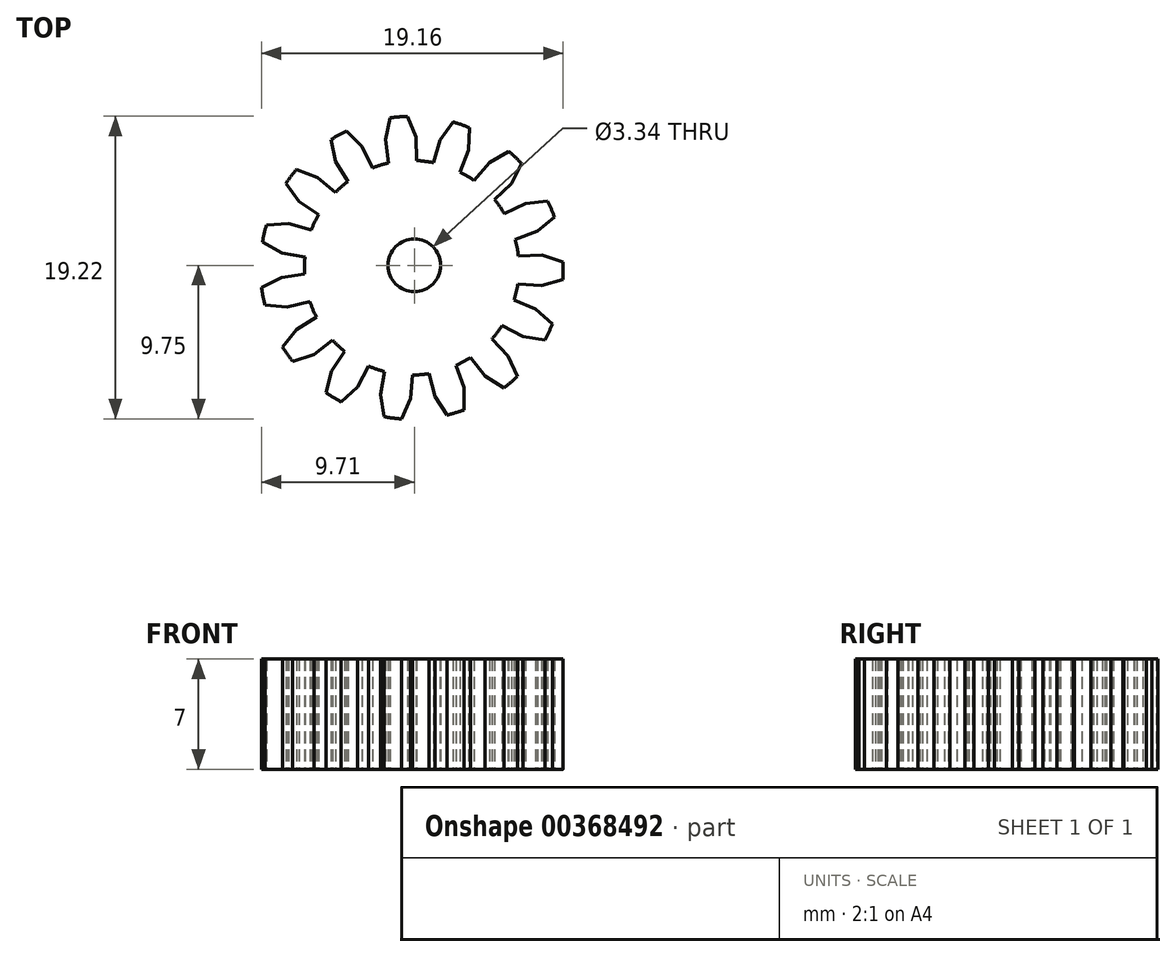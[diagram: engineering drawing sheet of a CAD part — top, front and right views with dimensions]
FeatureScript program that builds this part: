
annotation { "Feature Type Name" : "Feature", "Feature Type Description" : "" }
export const myFeature = defineFeature(function(context is Context, id is Id, definition is map)
    precondition{}
    {
        {
            var Q0;
            Q0=qCreatedBy(makeId("Top.planeOp"),FACE);
            var sketch = newSketch(context, id + "F0", { "sketchPlane" : qUnion([Q0])});
            skLineSegment(sketch, "E0", {"start": v(-0.17, -0.15) * mm, "end": v(4.15, 8.45) * mm, "construction": true});
            skLineSegment(sketch, "E1", {"start": v(-0.17, -0.15) * mm, "end": v(7.27, 5.95) * mm, "construction": true});
            skLineSegment(sketch, "E2", {"start": v(-0.17, -0.15) * mm, "end": v(6.41, 6.87) * mm, "construction": true});
            skLineSegment(sketch, "E3", {"start": v(5.1, 4.17) * mm, "end": v(6.17, 5.21) * mm});
            skLineSegment(sketch, "E4", {"start": v(6.17, 5.21) * mm, "end": v(6.8, 6.48) * mm});
            skLineSegment(sketch, "E5.MirrorCS", {"start": v(5.71, 3.3) * mm, "end": v(7.06, 3.94) * mm});
            skLineSegment(sketch, "E6.MirrorCS", {"start": v(4.77, 6.53) * mm, "end": v(5.99, 7.24) * mm});
            skArc(sketch, "E7", {"start": v(5.99, 7.24) * mm, "mid": v(6.41, 6.87) * mm, "end": v(6.8, 6.48) * mm});
            skLineSegment(sketch, "E8.1.0", {"start": v(6.6, 0.6) * mm, "end": v(8.1, 0.65) * mm});
            skLineSegment(sketch, "E8.1.1", {"start": v(7.06, 3.94) * mm, "end": v(8.46, 4.1) * mm});
            skLineSegment(sketch, "E8.1.2", {"start": v(7.8, 2.17) * mm, "end": v(8.9, 3.06) * mm});
            skArc(sketch, "E8.1.3", {"start": v(8.46, 4.1) * mm, "mid": v(8.7, 3.59) * mm, "end": v(8.9, 3.06) * mm});
            skLineSegment(sketch, "E8.1.4", {"start": v(6.4, 1.65) * mm, "end": v(7.8, 2.17) * mm});
            skArc(sketch, "E8.1.5", {"start": v(5.1, 4.17) * mm, "mid": v(5.42, 3.74) * mm, "end": v(5.71, 3.3) * mm});
            skLineSegment(sketch, "E8.2.0", {"start": v(6.33, -2.21) * mm, "end": v(7.7, -2.78) * mm});
            skLineSegment(sketch, "E8.2.1", {"start": v(8.1, 0.65) * mm, "end": v(9.45, 0.22) * mm});
            skLineSegment(sketch, "E8.2.2", {"start": v(8.06, -1.28) * mm, "end": v(9.42, -0.9) * mm});
            skArc(sketch, "E8.2.3", {"start": v(9.45, 0.22) * mm, "mid": v(9.45, -0.34) * mm, "end": v(9.42, -0.9) * mm});
            skLineSegment(sketch, "E8.2.4", {"start": v(6.57, -1.18) * mm, "end": v(8.06, -1.28) * mm});
            skArc(sketch, "E8.2.5", {"start": v(6.4, 1.65) * mm, "mid": v(6.52, 1.13) * mm, "end": v(6.6, 0.6) * mm});
            skLineSegment(sketch, "E8.3.0", {"start": v(4.93, -4.68) * mm, "end": v(5.96, -5.76) * mm});
            skLineSegment(sketch, "E8.3.1", {"start": v(7.7, -2.78) * mm, "end": v(8.77, -3.72) * mm});
            skLineSegment(sketch, "E8.3.2", {"start": v(6.9, -4.53) * mm, "end": v(8.3, -4.74) * mm});
            skArc(sketch, "E8.3.3", {"start": v(8.77, -3.72) * mm, "mid": v(8.54, -4.24) * mm, "end": v(8.3, -4.74) * mm});
            skLineSegment(sketch, "E8.3.4", {"start": v(5.57, -3.83) * mm, "end": v(6.9, -4.53) * mm});
            skArc(sketch, "E8.3.5", {"start": v(6.57, -1.18) * mm, "mid": v(6.47, -1.7) * mm, "end": v(6.33, -2.21) * mm});
            skLineSegment(sketch, "E8.4.0", {"start": v(2.65, -6.36) * mm, "end": v(3.15, -7.76) * mm});
            skLineSegment(sketch, "E8.4.1", {"start": v(5.96, -5.76) * mm, "end": v(6.54, -7.05) * mm});
            skLineSegment(sketch, "E8.4.2", {"start": v(4.5, -7.02) * mm, "end": v(5.7, -7.78) * mm});
            skArc(sketch, "E8.4.3", {"start": v(6.54, -7.05) * mm, "mid": v(6.13, -7.43) * mm, "end": v(5.7, -7.78) * mm});
            skLineSegment(sketch, "E8.4.4", {"start": v(3.58, -5.84) * mm, "end": v(4.5, -7.02) * mm});
            skArc(sketch, "E8.4.5", {"start": v(5.57, -3.83) * mm, "mid": v(5.27, -4.26) * mm, "end": v(4.93, -4.68) * mm});
            skLineSegment(sketch, "E8.5.0", {"start": v(-0.12, -6.96) * mm, "end": v(-0.24, -8.45) * mm});
            skLineSegment(sketch, "E8.5.1", {"start": v(3.15, -7.76) * mm, "end": v(3.16, -9.18) * mm});
            skLineSegment(sketch, "E8.5.2", {"start": v(1.3, -8.32) * mm, "end": v(2.08, -9.5) * mm});
            skArc(sketch, "E8.5.3", {"start": v(3.16, -9.18) * mm, "mid": v(2.62, -9.36) * mm, "end": v(2.08, -9.5) * mm});
            skLineSegment(sketch, "E8.5.4", {"start": v(0.94, -6.87) * mm, "end": v(1.3, -8.32) * mm});
            skArc(sketch, "E8.5.5", {"start": v(3.58, -5.84) * mm, "mid": v(3.12, -6.12) * mm, "end": v(2.65, -6.36) * mm});
            skLineSegment(sketch, "E8.6.0", {"start": v(-2.9, -6.4) * mm, "end": v(-3.6, -7.7) * mm});
            skLineSegment(sketch, "E8.6.1", {"start": v(-0.24, -8.45) * mm, "end": v(-0.8, -9.75) * mm});
            skLineSegment(sketch, "E8.6.2", {"start": v(-2.15, -8.22) * mm, "end": v(-1.92, -9.61) * mm});
            skArc(sketch, "E8.6.3", {"start": v(-0.8, -9.75) * mm, "mid": v(-1.36, -9.7) * mm, "end": v(-1.92, -9.61) * mm});
            skLineSegment(sketch, "E8.6.4", {"start": v(-1.9, -6.74) * mm, "end": v(-2.15, -8.22) * mm});
            skArc(sketch, "E8.6.5", {"start": v(0.94, -6.87) * mm, "mid": v(0.41, -6.94) * mm, "end": v(-0.12, -6.96) * mm});
            skLineSegment(sketch, "E8.7.0", {"start": v(-5.2, -4.74) * mm, "end": v(-6.38, -5.66) * mm});
            skLineSegment(sketch, "E8.7.1", {"start": v(-3.6, -7.7) * mm, "end": v(-4.65, -8.66) * mm});
            skLineSegment(sketch, "E8.7.2", {"start": v(-5.26, -6.71) * mm, "end": v(-5.61, -8.08) * mm});
            skArc(sketch, "E8.7.3", {"start": v(-4.65, -8.66) * mm, "mid": v(-5.14, -8.39) * mm, "end": v(-5.61, -8.08) * mm});
            skLineSegment(sketch, "E8.7.4", {"start": v(-4.42, -5.47) * mm, "end": v(-5.26, -6.71) * mm});
            skArc(sketch, "E8.7.5", {"start": v(-1.9, -6.74) * mm, "mid": v(-2.4, -6.59) * mm, "end": v(-2.9, -6.4) * mm});
            skLineSegment(sketch, "E8.anchor1", {"start": v(-0.17, -0.15) * mm, "end": v(5.71, 3.3) * mm, "construction": true});
            skLineSegment(sketch, "E8.anchor2", {"start": v(-0.17, -0.15) * mm, "end": v(-5.2, -4.74) * mm, "construction": true});
            skLineSegment(sketch, "E9.MirrorCS", {"start": v(3.8, 5.39) * mm, "end": v(4.77, 6.53) * mm});
            skLineSegment(sketch, "E10.MirrorCS", {"start": v(-6.38, -5.66) * mm, "end": v(-7.73, -6.1) * mm});
            skLineSegment(sketch, "E11.MirrorCS", {"start": v(-7.48, -4.08) * mm, "end": v(-8.37, -5.18) * mm});
            skLineSegment(sketch, "E12.MirrorCS", {"start": v(-6.22, -3.28) * mm, "end": v(-7.48, -4.08) * mm});
            skArc(sketch, "E13.MirrorCS", {"start": v(-6.95, 0.52) * mm, "mid": v(-6.98, -0.02) * mm, "end": v(-6.97, -0.55) * mm});
            skLineSegment(sketch, "E14.MirrorCS", {"start": v(-6.63, -2.3) * mm, "end": v(-8.09, -2.65) * mm});
            skLineSegment(sketch, "E15.MirrorCS", {"start": v(-8.09, -2.65) * mm, "end": v(-9.5, -2.51) * mm});
            skLineSegment(sketch, "E16.MirrorCS", {"start": v(-8.45, -0.76) * mm, "end": v(-9.7, -1.41) * mm});
            skLineSegment(sketch, "E17.MirrorCS", {"start": v(-6.97, -0.55) * mm, "end": v(-8.45, -0.76) * mm});
            skLineSegment(sketch, "E18.MirrorCS", {"start": v(-6.95, 0.52) * mm, "end": v(-8.42, 0.79) * mm});
            skLineSegment(sketch, "E19.MirrorCS", {"start": v(-8.42, 0.79) * mm, "end": v(-9.65, 1.48) * mm});
            skLineSegment(sketch, "E20.MirrorCS", {"start": v(-7.98, 2.66) * mm, "end": v(-9.4, 2.58) * mm});
            skLineSegment(sketch, "E21.MirrorCS", {"start": v(-6.54, 2.25) * mm, "end": v(-7.98, 2.66) * mm});
            skLineSegment(sketch, "E22.MirrorCS", {"start": v(-6.1, 3.22) * mm, "end": v(-7.32, 4.06) * mm});
            skLineSegment(sketch, "E23.MirrorCS", {"start": v(-7.32, 4.06) * mm, "end": v(-8.16, 5.2) * mm});
            skLineSegment(sketch, "E24.MirrorCS", {"start": v(-5.02, 4.64) * mm, "end": v(-6.16, 5.6) * mm});
            skLineSegment(sketch, "E25.MirrorCS", {"start": v(-6.16, 5.6) * mm, "end": v(-7.49, 6.1) * mm});
            skLineSegment(sketch, "E26.MirrorCS", {"start": v(-4.2, 5.33) * mm, "end": v(-5, 6.6) * mm});
            skLineSegment(sketch, "E27.MirrorCS", {"start": v(-5, 6.6) * mm, "end": v(-5.3, 7.99) * mm});
            skLineSegment(sketch, "E28.MirrorCS", {"start": v(-3.3, 7.54) * mm, "end": v(-4.31, 8.53) * mm});
            skLineSegment(sketch, "E29.MirrorCS", {"start": v(-2.65, 6.2) * mm, "end": v(-3.3, 7.54) * mm});
            skLineSegment(sketch, "E30.MirrorCS", {"start": v(-1.63, 6.5) * mm, "end": v(-1.83, 7.99) * mm});
            skLineSegment(sketch, "E31.MirrorCS", {"start": v(-1.83, 7.99) * mm, "end": v(-1.54, 9.37) * mm});
            skLineSegment(sketch, "E32.MirrorCS", {"start": v(0.1, 8.15) * mm, "end": v(-0.42, 9.47) * mm});
            skLineSegment(sketch, "E33.MirrorCS", {"start": v(0.15, 6.66) * mm, "end": v(0.1, 8.15) * mm});
            skLineSegment(sketch, "E34.MirrorCS", {"start": v(1.2, 6.52) * mm, "end": v(1.63, 7.96) * mm});
            skLineSegment(sketch, "E35.MirrorCS", {"start": v(1.63, 7.96) * mm, "end": v(2.45, 9.1) * mm});
            skLineSegment(sketch, "E36.MirrorCS", {"start": v(3.45, 7.33) * mm, "end": v(3.51, 8.74) * mm});
            skLineSegment(sketch, "E37.MirrorCS", {"start": v(2.89, 5.94) * mm, "end": v(3.45, 7.33) * mm});
            skArc(sketch, "E38", {"start": v(-1.54, 9.37) * mm, "mid": v(-0.98, 9.44) * mm, "end": v(-0.42, 9.47) * mm});
            skArc(sketch, "E39", {"start": v(0.15, 6.66) * mm, "mid": v(0.68, 6.61) * mm, "end": v(1.2, 6.52) * mm});
            skArc(sketch, "E40", {"start": v(2.45, 9.1) * mm, "mid": v(2.99, 8.94) * mm, "end": v(3.51, 8.74) * mm});
            skArc(sketch, "E41", {"start": v(-2.65, 6.2) * mm, "mid": v(-2.14, 6.37) * mm, "end": v(-1.63, 6.5) * mm});
            skArc(sketch, "E42", {"start": v(-5.3, 7.99) * mm, "mid": v(-4.81, 8.27) * mm, "end": v(-4.31, 8.53) * mm});
            skArc(sketch, "E43", {"start": v(-7.49, 6.1) * mm, "mid": v(-7.84, 5.66) * mm, "end": v(-8.16, 5.2) * mm});
            skArc(sketch, "E44", {"start": v(-5.02, 4.64) * mm, "mid": v(-4.63, 5) * mm, "end": v(-4.2, 5.33) * mm});
            skArc(sketch, "E45", {"start": v(-6.1, 3.22) * mm, "mid": v(-6.34, 2.74) * mm, "end": v(-6.54, 2.25) * mm});
            skArc(sketch, "E46", {"start": v(-9.4, 2.58) * mm, "mid": v(-9.54, 2.03) * mm, "end": v(-9.65, 1.48) * mm});
            skArc(sketch, "E47", {"start": v(-9.5, -2.51) * mm, "mid": v(-9.62, -1.97) * mm, "end": v(-9.7, -1.41) * mm});
            skArc(sketch, "E48", {"start": v(-7.73, -6.1) * mm, "mid": v(-8.06, -5.65) * mm, "end": v(-8.37, -5.18) * mm});
            skArc(sketch, "E49", {"start": v(2.89, 5.94) * mm, "mid": v(3.36, 5.68) * mm, "end": v(3.8, 5.39) * mm});
            skPoint(sketch, "E50.bottom.start.orphan", {"position": v(-0.17, -15.15) * mm});
            skPoint(sketch, "E51.bottom.start.orphan", {"position": v(-0.17, 14.85) * mm});
            skArc(sketch, "E52.trimOffspring", {"start": v(-6.63, -2.3) * mm, "mid": v(-6.45, -2.8) * mm, "end": v(-6.22, -3.28) * mm});
            skArc(sketch, "E53.trimOffspring", {"start": v(-4.42, -5.47) * mm, "mid": v(-4.83, -5.12) * mm, "end": v(-5.2, -4.74) * mm});
            skCircle(sketch, "E54", {"center": v(0, 0) * mm, "radius": 1.67 * mm});
            skSolve(sketch);
        }
        {
            var Q0;
            Q0=makeQuery(id+"F0.imprint","IMPRINT",FACE,{"disambiguationData":[TD([[makeQuery(id+"F0.imprint","IMPRINT",EDGE,{"derivedFrom":sQuery(id+"F0.wireOp",EDGE,"E3")}),1.0]])]});
            extrude(context, id + "F1", {"entities" : qUnion([Q0]), "depth" : 7 * mm});
        }
    });
